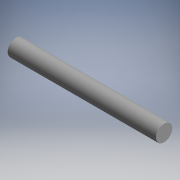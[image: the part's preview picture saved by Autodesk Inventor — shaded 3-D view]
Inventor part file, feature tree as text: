
AUTODESK INVENTOR PART (.ipt)
format: ipt  version: 2017.3 (Build 213256000, 256)  size: 100,864 bytes
history: native  units: mm (DEFAULTED — no unit token found)
features: other x7, revolve x1, sketch x1
ambient origin geometry x8: Origin, YZ Plane, XZ Plane, XY Plane, X Axis, Y Axis, Z Axis, Center Point
bodies: Solid1 (feature_tree)
feature tree (9):
  revolve  "Revolution1"  [1 undecoded]
  other  "COMBINATION_MODULE_XY"
  other  "COMBINATION_MODULE_YZ"
  other  "COMBINATION_MODULE_ZX"
  other  "COMBINATION_MODULE_X"
  other  "COMBINATION_MODULE_Y"
  other  "COMBINATION_MODULE_Z"
  other  "COMBINATION_MODULE_Center"
  sketch  "Sketch_1"  dims[d0=360.0deg d1=0.0mm]
note: 1 required parameter value undecoded (feature->parameter linkage not recoverable at this tier; creation-order binding heuristic only, values carry confidence <= 0.55)
